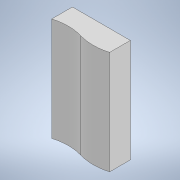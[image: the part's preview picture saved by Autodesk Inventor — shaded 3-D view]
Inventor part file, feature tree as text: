
AUTODESK INVENTOR PART (.ipt)
format: ipt  version: 2021 (Build 250183000, 183)  size: 107,520 bytes
history: native  units: mm
features: extrude x3, sketch x3, other x1
ambient origin geometry x8: Origin, YZ Plane, XZ Plane, XY Plane, X Axis, Y Axis, Z Axis, Center Point
bodies: Body1 (feature_tree)
feature tree (7):
  other  "ソリッド1"
  extrude  "押し出し1"  Depth=5000.0mm
  extrude  "押し出し2"  Depth=1000.0mm TaperAngle=0.0deg
  extrude  "押し出し3"  Depth=2000.0mm
  sketch  "スケッチ1"
  sketch  "スケッチ2"
  sketch  "スケッチ3"
